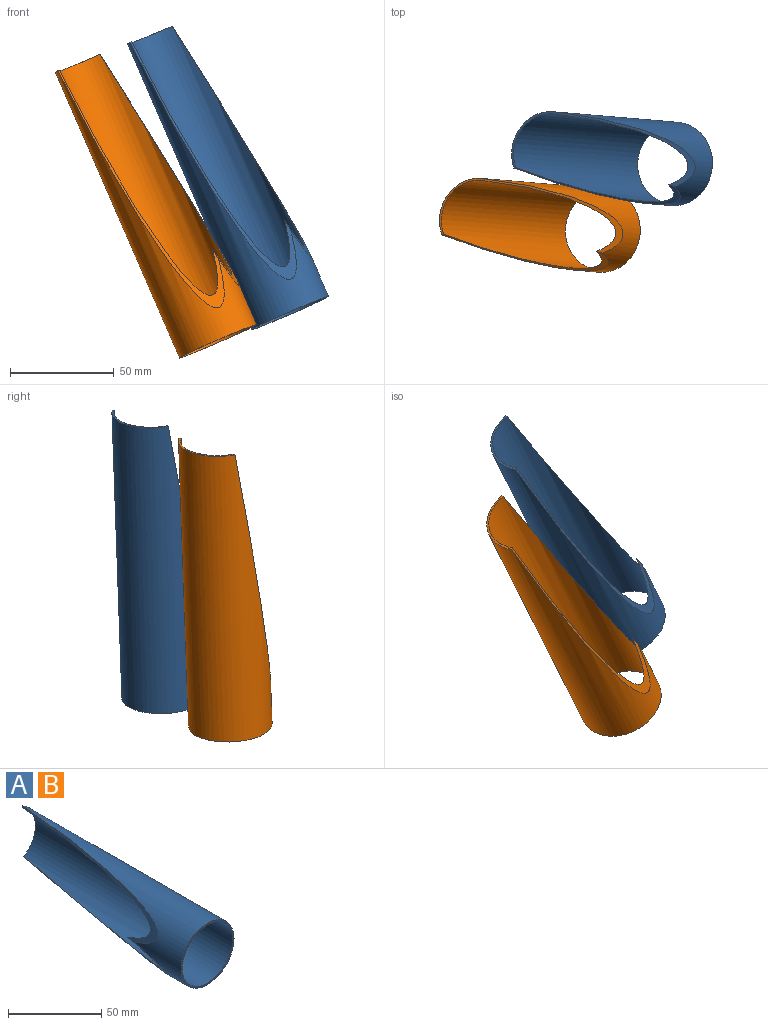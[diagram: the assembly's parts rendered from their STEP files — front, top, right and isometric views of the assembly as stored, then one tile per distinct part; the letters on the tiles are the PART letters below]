
ASSEMBLY  parts=2 mates=1
PART A: 6 faces, bbox 40.3x150x40.3 mm
  f0: cylinder r=19.15mm len=150mm, axis (0,1,0), area 10776.4mm2, adj f2,f3,f4,f5
  f1: cylinder r=20.15mm len=150mm, axis (0,1,0), area 10939.6mm2, adj f2,f3,f4,f5
  f2: plane 34.74x11.14mm, normal (0,1,0), area 40.9mm2, adj f0,f1,f4,f5
  f3: plane 40.3x40.3mm, normal (0,-1,0), area 123.5mm2, adj f0,f1
  f4: plane 129.51x29.63mm, normal (-0.87,0.15,0.46), area 263.4mm2, adj f0,f1,f2,f5
  f5: plane 135.78x31.03mm, normal (-0.83,0.15,-0.53), area 286.6mm2, adj f0,f1,f2,f4
PART B: same geometry as A
PLACE A rot(axis=(0.09,0.67,0.74),137.7deg) t=(-46.53,-46.49,20.2)mm
PLACE B rot(axis=(0.09,0.67,0.74),137.7deg) t=(-81.31,-78.56,6.55)mm
MATE parallel B.f2 <-> A.f2  axis (-0.4,0.03,0.92) through (-92.76,-68.26,1.22)mm
